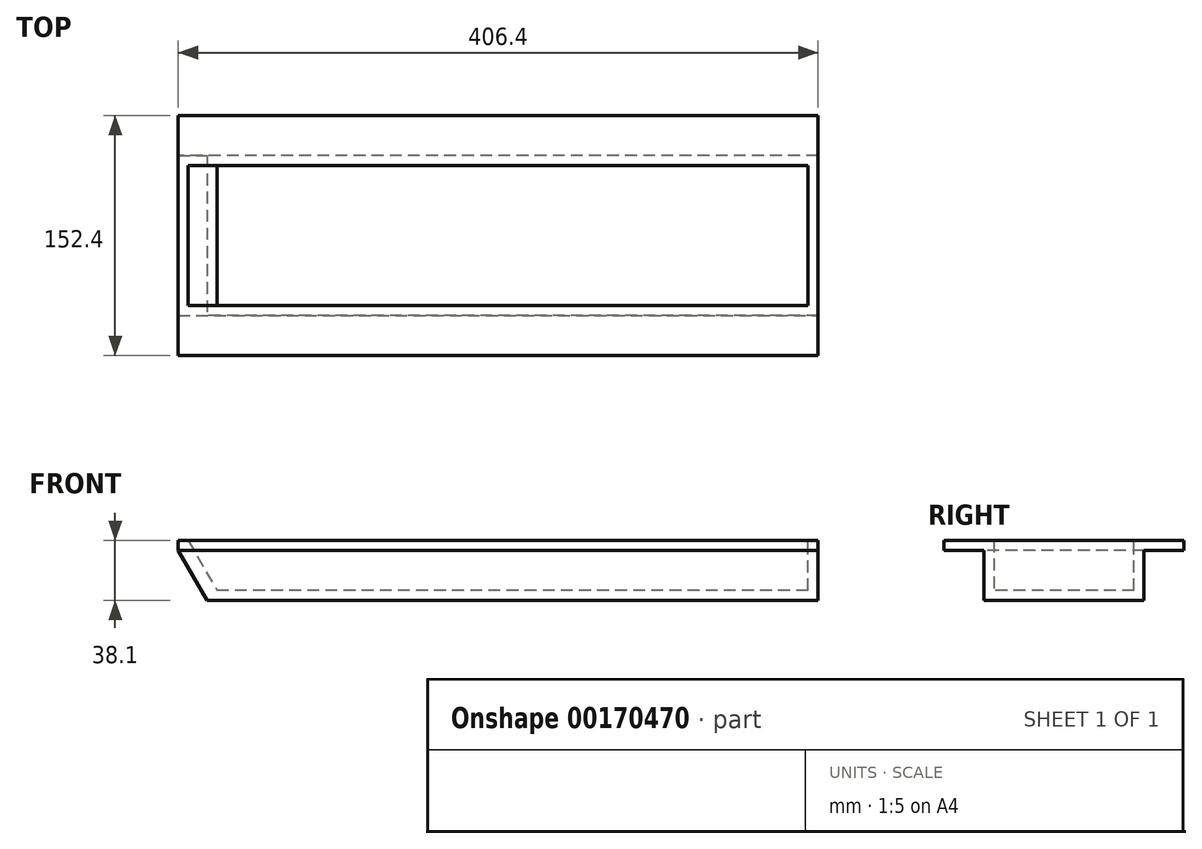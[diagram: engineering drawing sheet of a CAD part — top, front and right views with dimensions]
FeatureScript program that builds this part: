
annotation { "Feature Type Name" : "Feature", "Feature Type Description" : "" }
export const myFeature = defineFeature(function(context is Context, id is Id, definition is map)
    precondition{}
    {
        {
            var Q0;
            Q0=qCreatedBy(makeId("Right.planeOp"),FACE);
            var sketch = newSketch(context, id + "F0", { "sketchPlane" : qUnion([Q0])});
            skLineSegment(sketch, "E0.bottom", {"start": v(0, 0) * mm, "end": v(101.6, 0) * mm});
            skLineSegment(sketch, "E0.top", {"start": v(0, 38.1) * mm, "end": v(101.6, 38.1) * mm});
            skLineSegment(sketch, "E0.left", {"start": v(0, 0) * mm, "end": v(0, 38.1) * mm});
            skLineSegment(sketch, "E0.right", {"start": v(101.6, 0) * mm, "end": v(101.6, 38.1) * mm});
            skSolve(sketch);
        }
        {
            var Q0;
            Q0 = qSketchRegion(id + "F0", true);
            extrude(context, id + "F1", {"entities" : qUnion([Q0]), "depth" : 406.4 * mm, "offsetDistance" : 25.4 * mm, "symmetric" : true});
        }
        {
            var Q0;
            Q0=makeQuery(id+"F1.opExtrude","SWEPT_FACE",FACE,{"disambiguationData":[OSD([sQuery(id+"F0.wireOp",EDGE,"E0.left")])]});
            var sketch = newSketch(context, id + "F2", { "sketchPlane" : qUnion([Q0])});
            skLineSegment(sketch, "E1.bottom", {"start": v(-203.2, 38.1) * mm, "end": v(203.2, 38.1) * mm});
            skLineSegment(sketch, "E1.top", {"start": v(-203.2, 31.75) * mm, "end": v(203.2, 31.75) * mm});
            skLineSegment(sketch, "E1.left", {"start": v(-203.2, 38.1) * mm, "end": v(-203.2, 31.75) * mm});
            skLineSegment(sketch, "E1.right", {"start": v(203.2, 38.1) * mm, "end": v(203.2, 31.75) * mm});
            skSolve(sketch);
        }
        {
            var Q0;
            Q0=makeQuery(id+"F1.opExtrude","SWEPT_FACE",FACE,{"disambiguationData":[OSD([sQuery(id+"F0.wireOp",EDGE,"E0.top")])]});
            shell(context, id + "F3", {"entities" : qUnion([Q0]), "thickness" : 6.35 * mm});
        }
        {
            var Q0;
            Q0=makeQuery(id+"F2.imprint","IMPRINT",FACE,{"disambiguationData":[TD([[makeQuery(id+"F2.imprint","IMPRINT",EDGE,{"derivedFrom":sQuery(id+"F2.wireOp",EDGE,"E1.bottom")}),1.0]])]});
            extrude(context, id + "F4", {"entities" : qUnion([Q0]), "operationType" : NewBodyOperationType.ADD, "depth" : 25.4 * mm, "offsetDistance" : 25.4 * mm});
        }
        {
            var Q0;
            Q0=makeQuery(id+"F1.opExtrude","SWEPT_FACE",FACE,{"disambiguationData":[OSD([sQuery(id+"F0.wireOp",EDGE,"E0.right")])]});
            var sketch = newSketch(context, id + "F5", { "sketchPlane" : qUnion([Q0])});
            skLineSegment(sketch, "E2.bottom", {"start": v(-203.2, 38.1) * mm, "end": v(203.2, 38.1) * mm});
            skLineSegment(sketch, "E2.top", {"start": v(-203.2, 31.75) * mm, "end": v(203.2, 31.75) * mm});
            skLineSegment(sketch, "E2.left", {"start": v(-203.2, 38.1) * mm, "end": v(-203.2, 31.75) * mm});
            skLineSegment(sketch, "E2.right", {"start": v(203.2, 38.1) * mm, "end": v(203.2, 31.75) * mm});
            skSolve(sketch);
        }
        {
            var Q0;
            Q0 = qSketchRegion(id + "F5", true);
            extrude(context, id + "F6", {"entities" : qUnion([Q0]), "operationType" : NewBodyOperationType.ADD, "depth" : 25.4 * mm, "offsetDistance" : 25.4 * mm});
        }
        {
            var Q0;
            Q0=makeQuery(id+"F3.opShell","OFFSET_FACE",FACE,{"disambiguationData":[OSD([sQuery(id+"F0.wireOp",EDGE,"E0.left")])]});
            var sketch = newSketch(context, id + "F7", { "sketchPlane" : qUnion([Q0])});
            skLineSegment(sketch, "E3", {"start": v(196.85, 38.1) * mm, "end": v(178.52, 6.35) * mm});
            skLineSegment(sketch, "E4", {"start": v(178.52, 6.35) * mm, "end": v(196.85, 6.35) * mm});
            skLineSegment(sketch, "E5", {"start": v(196.85, 6.35) * mm, "end": v(196.85, 38.1) * mm});
            skSolve(sketch);
        }
        {
            var Q0;
            Q0=makeQuery(id+"F7.imprint","IMPRINT",FACE,{"disambiguationData":[TD([[makeQuery(id+"F7.imprint","IMPRINT",EDGE,{"derivedFrom":sQuery(id+"F7.wireOp",EDGE,"E3")}),1.0]])]});
            extrude(context, id + "F8", {"entities" : qUnion([Q0]), "operationType" : NewBodyOperationType.ADD, "endBound" : BoundingType.UP_TO_NEXT, "depth" : 72.14 * mm, "offsetDistance" : 25.4 * mm});
        }
        {
            var Q0;
            Q0=qCreatedBy(makeId("Front.planeOp"),FACE);
            var sketch = newSketch(context, id + "F9", { "sketchPlane" : qUnion([Q0])});
            skLineSegment(sketch, "E6", {"start": v(-203.2, 36.4) * mm, "end": v(-203.2, 0) * mm});
            skLineSegment(sketch, "E7", {"start": v(-203.2, 0) * mm, "end": v(-182.19, 0) * mm});
            skLineSegment(sketch, "E8", {"start": v(-182.19, 0) * mm, "end": v(-203.2, 36.4) * mm});
            skLineSegment(sketch, "E9", {"start": v(-200.52, 31.75) * mm, "end": v(-203.2, 31.75) * mm});
            skLineSegment(sketch, "E10", {"start": v(-203.2, 31.75) * mm, "end": v(-184.87, 0) * mm});
            skSolve(sketch);
        }
        {
            var Q0;
            {var subQ2=sQuery(id+"F9.wireOp",EDGE,"E7");Q0=makeQuery(id+"F9.imprint","IMPRINT",FACE,{"disambiguationData":[TD([[makeQuery(id+"F9.imprint","IMPRINT",EDGE,{"derivedFrom":subQ2}),1.0]])]});}
            extrude(context, id + "F10", {"entities" : qUnion([Q0]), "operationType" : NewBodyOperationType.REMOVE, "oppositeDirection" : true, "depth" : 141.22 * mm, "offsetDistance" : 25.4 * mm});
        }
    });
